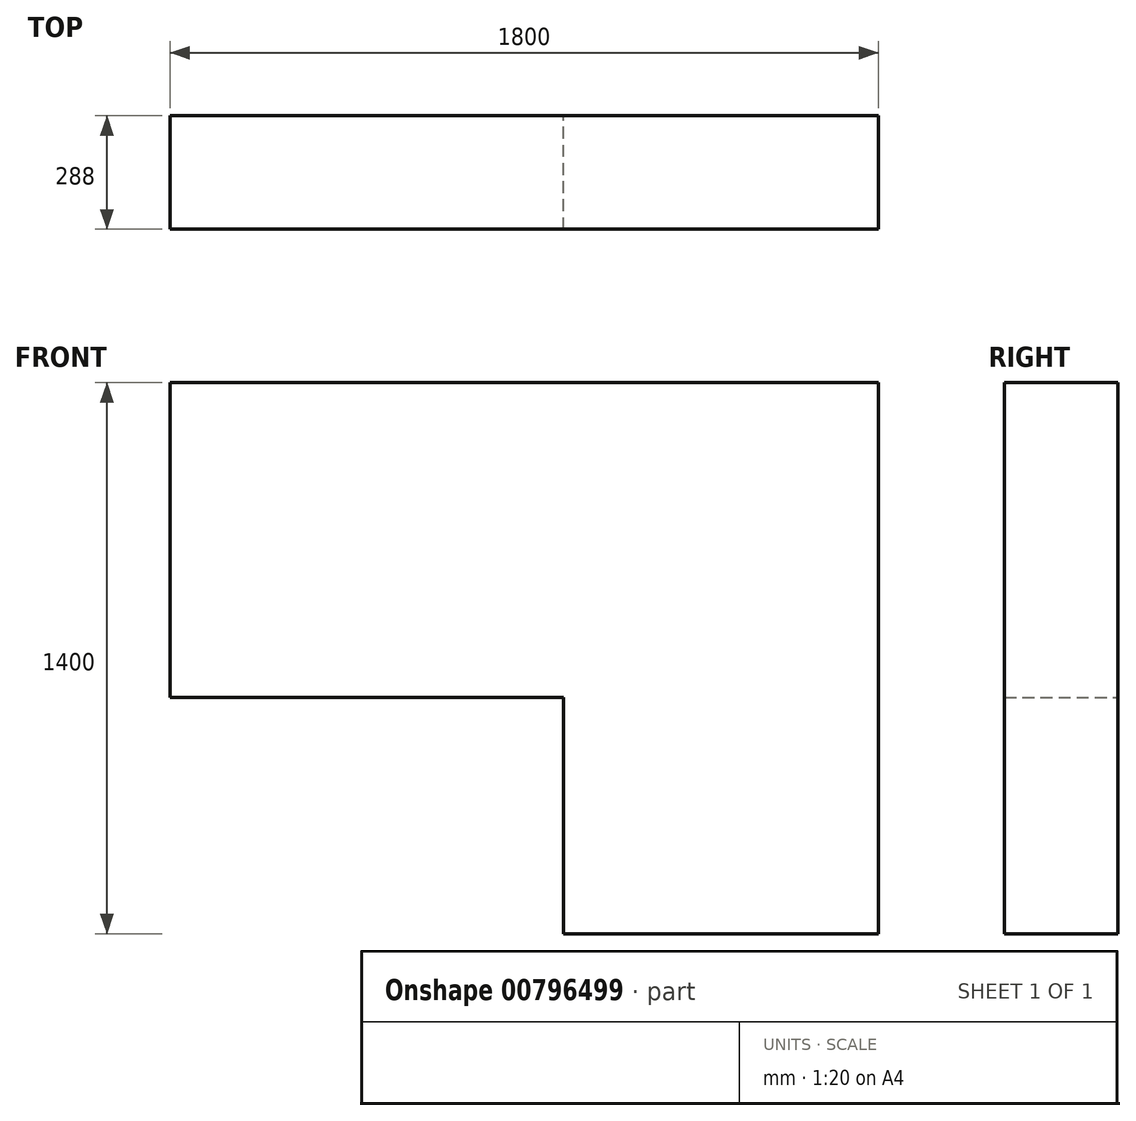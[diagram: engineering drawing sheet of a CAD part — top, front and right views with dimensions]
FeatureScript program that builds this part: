
annotation { "Feature Type Name" : "Feature", "Feature Type Description" : "" }
export const myFeature = defineFeature(function(context is Context, id is Id, definition is map)
    precondition{}
    {
        {
            var Q0;
            Q0=qCreatedBy(makeId("Front.planeOp"),FACE);
            var sketch = newSketch(context, id + "F0", { "sketchPlane" : qUnion([Q0])});
            skLineSegment(sketch, "E0", {"start": v(395.49, 530.78) * mm, "end": v(1595.49, 530.78) * mm});
            skLineSegment(sketch, "E1", {"start": v(1595.49, 530.78) * mm, "end": v(1595.49, -269.22) * mm});
            skLineSegment(sketch, "E2", {"start": v(395.49, -269.22) * mm, "end": v(1595.49, -269.22) * mm});
            skLineSegment(sketch, "E3", {"start": v(395.49, 530.78) * mm, "end": v(395.49, -269.22) * mm});
            skLineSegment(sketch, "E4", {"start": v(395.49, 530.78) * mm, "end": v(-204.51, 530.78) * mm});
            skLineSegment(sketch, "E5", {"start": v(-204.51, 530.78) * mm, "end": v(-204.51, -269.22) * mm});
            skLineSegment(sketch, "E6", {"start": v(-204.51, -269.22) * mm, "end": v(395.49, -269.22) * mm});
            skLineSegment(sketch, "E7", {"start": v(1595.49, -269.22) * mm, "end": v(1595.49, -869.22) * mm});
            skLineSegment(sketch, "E8", {"start": v(1595.49, -869.22) * mm, "end": v(795.49, -869.22) * mm});
            skLineSegment(sketch, "E9", {"start": v(795.49, -869.22) * mm, "end": v(795.49, -269.22) * mm});
            skSolve(sketch);
        }
        {
            var Q0;
            Q0=makeQuery(id+"F0.imprint","IMPRINT",FACE,{"disambiguationData":[TD([[makeQuery(id+"F0.imprint","IMPRINT",EDGE,{"derivedFrom":sQuery(id+"F0.wireOp",EDGE,"E3")}),-1.0]])]});
            var Q1;
            {var subQ0=sQuery(id+"F0.wireOp",EDGE,"E7");Q1=makeQuery(id+"F0.imprint","IMPRINT",FACE,{"disambiguationData":[TD([[makeQuery(id+"F0.imprint","IMPRINT",EDGE,{"derivedFrom":subQ0}),-1.0]])]});}
            var Q2;
            Q2=makeQuery(id+"F0.imprint","IMPRINT",FACE,{"disambiguationData":[TD([[makeQuery(id+"F0.imprint","IMPRINT",EDGE,{"derivedFrom":sQuery(id+"F0.wireOp",EDGE,"E0")}),-1.0]])]});
            extrude(context, id + "F1", {"entities" : qUnion([Q0, Q1, Q2]), "depth" : 288 * mm, "offsetDistance" : 25 * mm});
        }
    });
